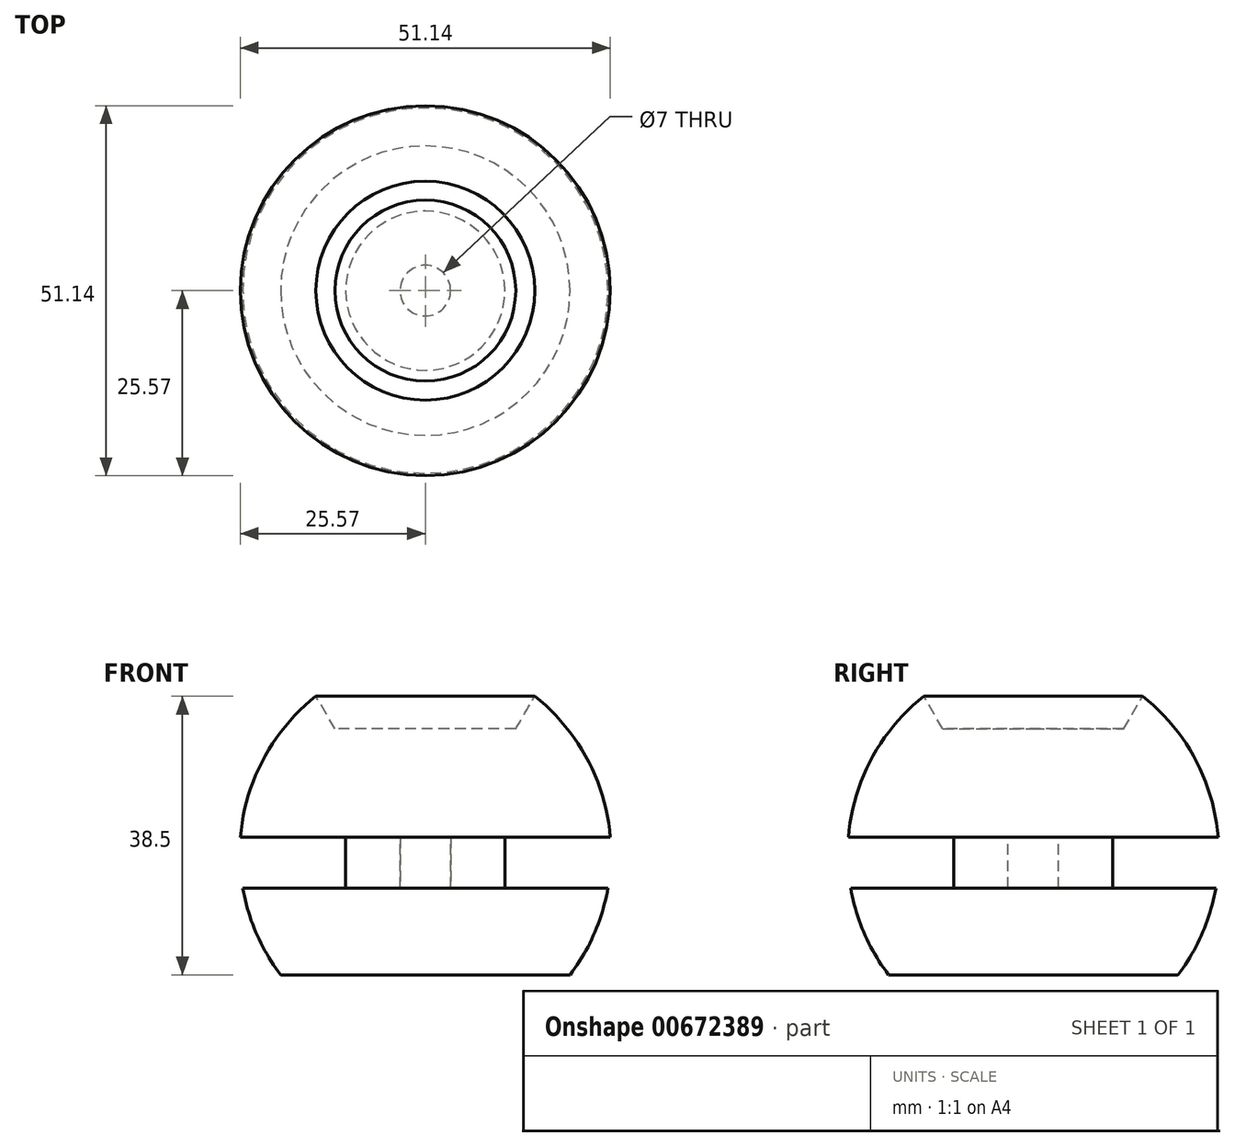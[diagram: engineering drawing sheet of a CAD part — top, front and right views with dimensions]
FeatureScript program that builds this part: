
annotation { "Feature Type Name" : "Feature", "Feature Type Description" : "" }
export const myFeature = defineFeature(function(context is Context, id is Id, definition is map)
    precondition{}
    {
        {
            var Q0;
            Q0=qCreatedBy(makeId("Front.planeOp"),FACE);
            var sketch = newSketch(context, id + "F0", { "sketchPlane" : qUnion([Q0])});
            skLineSegment(sketch, "E0", {"start": v(0, -12) * mm, "end": v(20, -12) * mm});
            skLineSegment(sketch, "E1", {"start": v(0, 22) * mm, "end": v(12.5, 22) * mm});
            skLineSegment(sketch, "E2", {"start": v(12.5, 22) * mm, "end": v(15.13, 26.5) * mm});
            skArc(sketch, "E3", {"start": v(20, -12) * mm, "mid": v(25.44, 8.25) * mm, "end": v(15.13, 26.5) * mm});
            skLineSegment(sketch, "E4", {"start": v(0, 22) * mm, "end": v(0, -12) * mm});
            skSolve(sketch);
        }
        {
            var Q0;
            Q0=qCreatedBy(makeId("Front.planeOp"),FACE);
            var sketch = newSketch(context, id + "F1", { "sketchPlane" : qUnion([Q0])});
            skLineSegment(sketch, "E5.bottom", {"start": v(3.5, 7) * mm, "end": v(11, 7) * mm});
            skLineSegment(sketch, "E5.top", {"start": v(3.5, 0) * mm, "end": v(11, 0) * mm});
            skLineSegment(sketch, "E5.left", {"start": v(3.5, 7) * mm, "end": v(3.5, 0) * mm});
            skLineSegment(sketch, "E5.right", {"start": v(11, 7) * mm, "end": v(11, 0) * mm});
            skSolve(sketch);
        }
        {
            var Q0;
            Q0=qCreatedBy(makeId("Front.planeOp"),FACE);
            var sketch = newSketch(context, id + "F2", { "sketchPlane" : qUnion([Q0])});
            skLineSegment(sketch, "E6.bottom", {"start": v(3.5, 0) * mm, "end": v(28.7, 0) * mm});
            skLineSegment(sketch, "E6.top", {"start": v(3.5, 7) * mm, "end": v(28.7, 7) * mm});
            skLineSegment(sketch, "E6.left", {"start": v(3.5, 0) * mm, "end": v(3.5, 7) * mm});
            skLineSegment(sketch, "E6.right", {"start": v(28.7, 0) * mm, "end": v(28.7, 7) * mm});
            skSolve(sketch);
        }
        {
            var Q0;
            Q0=makeQuery(id+"F0.imprint","IMPRINT",FACE,{"disambiguationData":[TD([[makeQuery(id+"F0.imprint","IMPRINT",EDGE,{"derivedFrom":sQuery(id+"F0.wireOp",EDGE,"E0")}),1.0]])]});
            var Q1;
            Q1=sQuery(id+"F0.wireOp",EDGE,"E4");
            revolve(context, id + "F3", {"entities" : qUnion([Q0]), "axis" : qUnion([Q1]), "revolveType" : RevolveType.FULL});
        }
        {
            var Q0;
            Q0=makeQuery(id+"F2.imprint","IMPRINT",FACE,{"disambiguationData":[TD([[makeQuery(id+"F2.imprint","IMPRINT",EDGE,{"derivedFrom":sQuery(id+"F2.wireOp",EDGE,"E6.bottom")}),1.0]])]});
            var Q1;
            Q1=sQuery(id+"F0.wireOp",EDGE,"E4");
            revolve(context, id + "F4", {"operationType" : NewBodyOperationType.REMOVE, "entities" : qUnion([Q0]), "axis" : qUnion([Q1]), "revolveType" : RevolveType.FULL, "oppositeDirection" : true});
        }
        {
            var Q0;
            Q0 = qSketchRegion(id + "F1", true);
            var Q1;
            Q1=sQuery(id+"F0.wireOp",EDGE,"E4");
            revolve(context, id + "F5", {"entities" : qUnion([Q0]), "axis" : qUnion([Q1]), "revolveType" : RevolveType.FULL});
        }
    });
